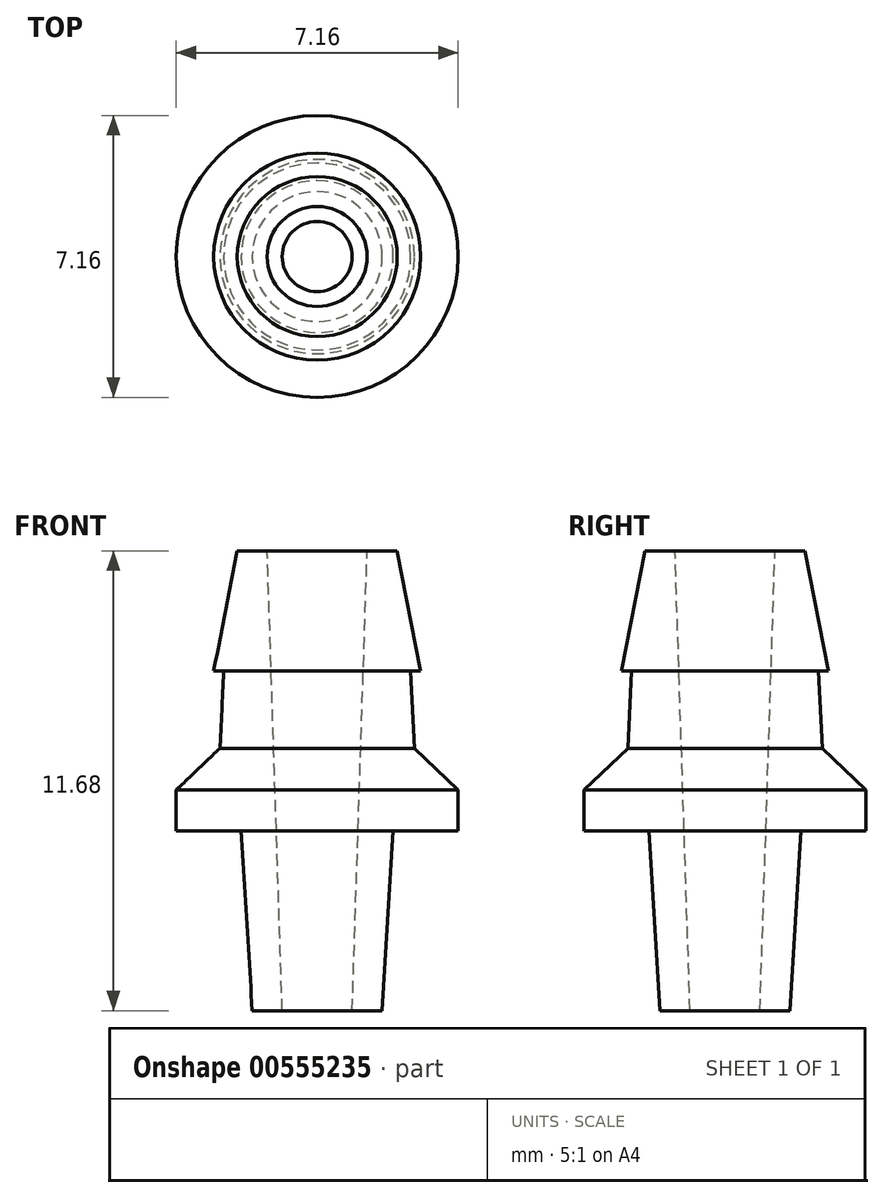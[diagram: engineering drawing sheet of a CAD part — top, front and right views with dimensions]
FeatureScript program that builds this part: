
annotation { "Feature Type Name" : "Feature", "Feature Type Description" : "" }
export const myFeature = defineFeature(function(context is Context, id is Id, definition is map)
    precondition{}
    {
        {
            var Q0;
            Q0=qCreatedBy(makeId("Front.planeOp"),FACE);
            var sketch = newSketch(context, id + "F0", { "sketchPlane" : qUnion([Q0])});
            skLineSegment(sketch, "E0", {"start": v(0, 0) * mm, "end": v(0, 3.56) * mm, "construction": true});
            skLineSegment(sketch, "E1", {"start": v(1.93, 0) * mm, "end": v(0, 0) * mm, "construction": true});
            skLineSegment(sketch, "E2", {"start": v(1.65, -4.57) * mm, "end": v(1.93, 0) * mm});
            skLineSegment(sketch, "E3", {"start": v(3.58, 0) * mm, "end": v(3.58, 0.89) * mm});
            skLineSegment(sketch, "E4", {"start": v(1.65, -4.57) * mm, "end": v(0.89, -4.57) * mm});
            skLineSegment(sketch, "E5", {"start": v(1.93, 0) * mm, "end": v(3.58, 0) * mm});
            skLineSegment(sketch, "E6", {"start": v(3.58, 0.89) * mm, "end": v(2.53, 0.89) * mm});
            skLineSegment(sketch, "E7", {"start": v(2.53, 0.89) * mm, "end": v(2.37, 4.06) * mm});
            skLineSegment(sketch, "E8", {"start": v(2.37, 4.06) * mm, "end": v(2.63, 4.06) * mm});
            skLineSegment(sketch, "E9", {"start": v(2.63, 4.06) * mm, "end": v(2.03, 7.11) * mm});
            skLineSegment(sketch, "E10", {"start": v(2.03, 7.11) * mm, "end": v(1.27, 7.11) * mm});
            skLineSegment(sketch, "E11", {"start": v(0.89, -4.57) * mm, "end": v(1.27, 7.11) * mm});
            skCircle(sketch, "E12", {"center": v(2.7, -0.83) * mm, "radius": 0.83 * mm, "construction": true});
            skLineSegment(sketch, "E13", {"start": v(2.7, -1.65) * mm, "end": v(1.83, -1.65) * mm, "construction": true});
            skSolve(sketch);
        }
        {
            var Q0;
            Q0 = qSketchRegion(id + "F0", true);
            var Q1;
            Q1=sQuery(id+"F0.wireOp",EDGE,"E0");
            revolve(context, id + "F1", {"entities" : qUnion([Q0]), "axis" : qUnion([Q1]), "revolveType" : RevolveType.FULL});
        }
        {
            var Q0;
            Q0=makeQuery(id+"F1.opRevolve","SWEPT_EDGE",EDGE,{"disambiguationData":[OSD([sQuery(id+"F0.wireOp",EDGE,"E6"),sQuery(id+"F0.wireOp",EDGE,"E7")])]});
            chamfer(context, id + "F2", {"entities" : qUnion([Q0]), "width" : 1.27 * mm, "tangentPropagation" : true});
        }
    });
